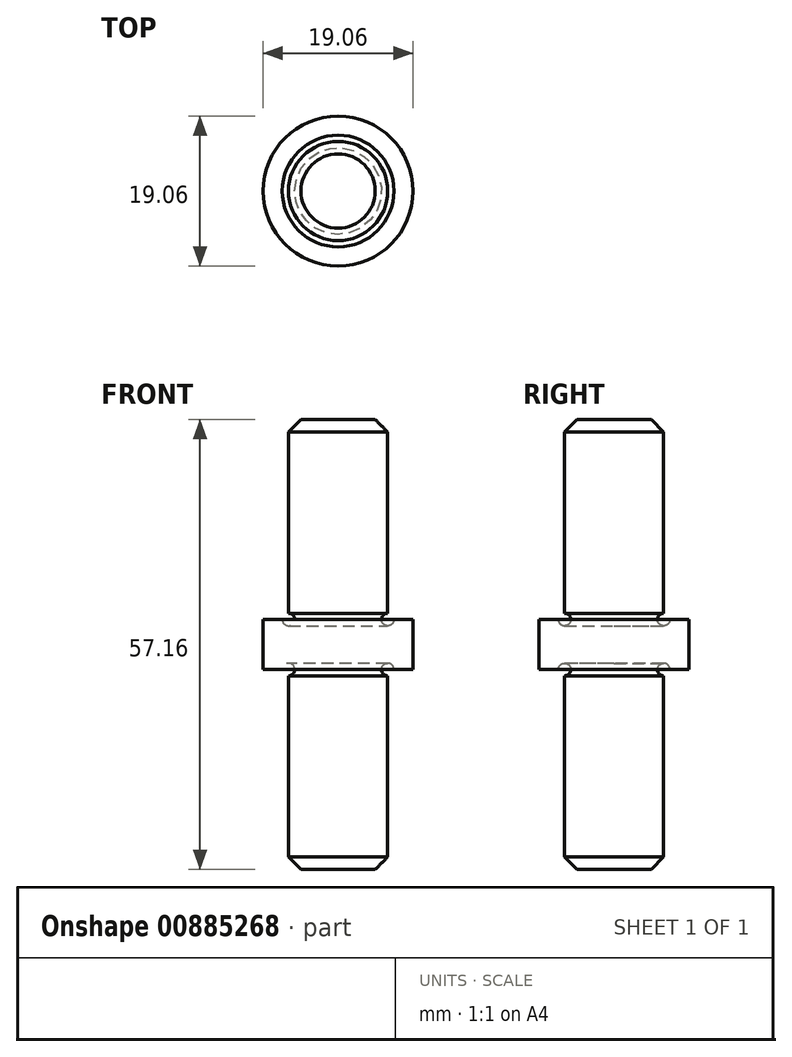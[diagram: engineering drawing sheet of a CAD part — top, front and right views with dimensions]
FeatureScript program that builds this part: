
annotation { "Feature Type Name" : "Feature", "Feature Type Description" : "" }
export const myFeature = defineFeature(function(context is Context, id is Id, definition is map)
    precondition{}
    {
        {
            var Q0;
            Q0=qCreatedBy(makeId("Front.planeOp"),FACE);
            var sketch = newSketch(context, id + "F0", { "sketchPlane" : qUnion([Q0])});
            skLineSegment(sketch, "E0", {"start": v(-9.53, 0) * mm, "end": v(-9.53, -3.18) * mm});
            skLineSegment(sketch, "E1", {"start": v(-9.53, -3.18) * mm, "end": v(-6.3, -3.18) * mm});
            skLineSegment(sketch, "E2", {"start": v(-6.3, -3.18) * mm, "end": v(-6.3, -28.58) * mm});
            skLineSegment(sketch, "E3", {"start": v(-6.3, -28.58) * mm, "end": v(0, -28.58) * mm});
            skLineSegment(sketch, "E4", {"start": v(0, -28.58) * mm, "end": v(0, 0) * mm});
            skLineSegment(sketch, "E5", {"start": v(0, 0) * mm, "end": v(-9.53, 0) * mm});
            skCircle(sketch, "E6", {"center": v(-6.3, -3.18) * mm, "radius": 0.8 * mm});
            skLineSegment(sketch, "E7.MirrorCS", {"start": v(-9.53, 0) * mm, "end": v(-9.53, 3.18) * mm});
            skLineSegment(sketch, "E8.MirrorCS", {"start": v(-9.53, 3.18) * mm, "end": v(-6.3, 3.18) * mm});
            skCircle(sketch, "E9.MirrorC", {"center": v(-6.3, 3.18) * mm, "radius": 0.8 * mm});
            skLineSegment(sketch, "E10.MirrorCS", {"start": v(-6.3, 3.18) * mm, "end": v(-6.3, 28.58) * mm});
            skLineSegment(sketch, "E11.MirrorCS", {"start": v(-6.3, 28.58) * mm, "end": v(0, 28.58) * mm});
            skLineSegment(sketch, "E12.MirrorCS", {"start": v(0, 28.58) * mm, "end": v(0, 0) * mm});
            skSolve(sketch);
        }
        {
            var Q0;
            Q0=makeQuery(id+"F0.imprint","IMPRINT",FACE,{"disambiguationData":[TD([[makeQuery(id+"F0.imprint","IMPRINT",EDGE,{"derivedFrom":sQuery(id+"F0.wireOp",EDGE,"E5")}),-1.0]])]});
            var Q1;
            {var subQ5=sQuery(id+"F0.wireOp",EDGE,"E0");Q1=makeQuery(id+"F0.imprint","IMPRINT",FACE,{"disambiguationData":[TD([[makeQuery(id+"F0.imprint","IMPRINT",EDGE,{"derivedFrom":subQ5}),1.0]])]});}
            var Q2;
            Q2=sQuery(id+"F0.wireOp",EDGE,"E4");
            revolve(context, id + "F1", {"surfaceOperationType" : NewSurfaceOperationType.NEW, "entities" : qUnion([Q0, Q1]), "axis" : qUnion([Q2]), "revolveType" : RevolveType.FULL});
        }
        {
            var Q0;
            Q0=makeQuery(id+"F1.opRevolve","SWEPT_EDGE",EDGE,{"disambiguationData":[OSD([sQuery(id+"F0.wireOp",EDGE,"E10.MirrorCS"),sQuery(id+"F0.wireOp",EDGE,"E11.MirrorCS")])]});
            var Q1;
            Q1=makeQuery(id+"F1.opRevolve","SWEPT_EDGE",EDGE,{"disambiguationData":[OSD([sQuery(id+"F0.wireOp",EDGE,"E2"),sQuery(id+"F0.wireOp",EDGE,"E3")])]});
            chamfer(context, id + "F2", {"entities" : qUnion([Q0, Q1]), "width" : 1.59 * mm, "tangentPropagation" : true});
        }
    });
